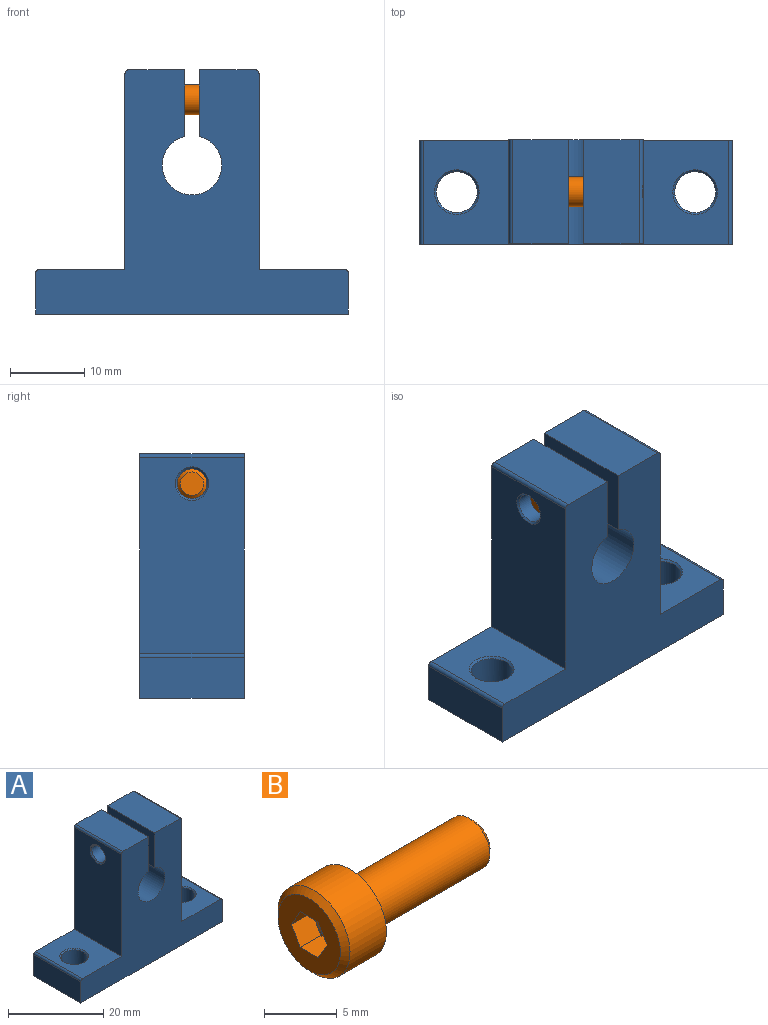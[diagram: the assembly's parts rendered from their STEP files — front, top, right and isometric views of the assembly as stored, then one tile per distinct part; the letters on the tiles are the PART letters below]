
ASSEMBLY  parts=2 mates=1
PART A: 30 faces, bbox 42x14x32.8 mm
  f0: cylinder r=2mm len=4mm, axis (1,0,0), area 50.3mm2, adj f11,f22
  f1: plane 42x14mm, normal (0,0,-1), area 531.5mm2, adj f6,f7,f13,f14,f27,f28
  f2: plane 14x8.93mm, normal (1,0,0), area 112.4mm2, adj f3,f12,f13,f14,f17
  f3: plane 14x7.5mm, normal (0,0,1), area 105mm2, adj f2,f13,f14,f18
  f4: plane 26.3x14mm, normal (-1,0,0), area 352.3mm2, adj f5,f13,f14,f18,f26
  f5: plane 14x11.5mm, normal (0,0,1), area 132.7mm2, adj f4,f13,f14,f19,f25
  f6: plane 14x5.5mm, normal (-1,0,0), area 77mm2, adj f1,f13,f14,f19
  f7: plane 14x5.5mm, normal (1,0,0), area 77mm2, adj f1,f13,f14,f20
  f8: plane 14x11.5mm, normal (0,0,1), area 132.7mm2, adj f9,f13,f14,f20,f24
  f9: plane 26.3x14mm, normal (1,0,0), area 324.5mm2, adj f8,f13,f14,f21,f29
  f10: plane 14x7.5mm, normal (0,0,1), area 105mm2, adj f11,f13,f14,f21
  f11: plane 14x8.93mm, normal (-1,0,0), area 112.4mm2, adj f0,f10,f12,f13,f14
  f12: cylinder r=4mm len=14mm, axis (0,1,0), area 323.6mm2, adj f2,f11,f13,f14
  f13: plane 42x32.8mm, normal (0,-1,0), area 666.2mm2, adj f1,f2,f3,f4,f5,f6,f7,f8
  f14: plane 42x32.8mm, normal (0,1,0), area 666.2mm2, adj f1,f2,f3,f4,f5,f6,f7,f8
  f15: cylinder r=2.75mm len=5.5mm, axis (0,0,-1), area 95mm2, adj f24,f28
  f16: cylinder r=2.75mm len=5.5mm, axis (0,0,-1), area 95mm2, adj f25,f27
  f17: cylinder r=2mm len=7.75mm, axis (1,0,0), area 97.4mm2, adj f2,f26
  f18: cylinder r=0.5mm len=14mm, axis (0,1,0), area 11mm2, adj f3,f4,f13,f14
  f19: cylinder r=0.5mm len=14mm, axis (0,1,0), area 11mm2, adj f5,f6,f13,f14
  f20: cylinder r=0.5mm len=14mm, axis (0,1,0), area 11mm2, adj f7,f8,f13,f14
  f21: cylinder r=0.5mm len=14mm, axis (0,1,0), area 10.6mm2, adj f9,f10,f13,f14,f29
  f22: plane 7x7mm, normal (1,0,0), area 25.9mm2, adj f0,f23
  f23: cylinder r=3.5mm len=7mm, axis (1,0,0), area 82.5mm2, adj f22,f29
  f24: cone r=3mm half-angle=45deg, axis (0,0,1), area 6.4mm2, adj f8,f15
  f25: cone r=3mm half-angle=45deg, axis (0,0,1), area 6.4mm2, adj f5,f16
  f26: cone r=2.25mm half-angle=45deg, axis (-1,0,0), area 4.7mm2, adj f4,f17
  f27: cone r=2.75mm half-angle=45deg, axis (0,0,-1), area 6.4mm2, adj f1,f16
  f28: cone r=3mm half-angle=45deg, axis (0,0,-1), area 6.4mm2, adj f1,f15
  f29: cone r=3.5mm half-angle=45deg, axis (1,0,0), area 8mm2, adj f9,f21,f23
PART B: 21 faces, bbox 16x7x7 mm
  f0: plane 6.07x6.07mm, normal (-1,0,0), area 21.1mm2, adj f1,f13,f14,f15,f16,f17,f18
  f1: cone r=3.03mm half-angle=45deg, axis (1,0,0), area 13.5mm2, adj f0,f2
  f2: cylinder r=3.5mm len=7mm, axis (1,0,0), area 77.7mm2, adj f1,f3
  f3: plane 7x7mm, normal (1,0,0), area 25.9mm2, adj f2,f4
  f4: cylinder r=2mm len=11.57mm, axis (1,0,0), area 145.4mm2, adj f3,f5
  f5: cone r=2mm half-angle=45deg, axis (-1,0,0), area 6.8mm2, adj f4,f6
  f6: plane 3.14x3.14mm, normal (1,0,0), area 7.7mm2, adj f5
  f7: plane 1.3x0.75mm, normal (-1,0,0), area 0.1mm2, adj f15,f16,f20
  f8: plane 1.5x0.43mm, normal (-1,0,0), area 0.1mm2, adj f14,f15,f20
  f9: plane 1.3x0.75mm, normal (-1,0,0), area 0.1mm2, adj f13,f14,f20
  f10: plane 1.3x0.75mm, normal (-1,0,0), area 0.1mm2, adj f13,f18,f20
  f11: plane 1.5x0.43mm, normal (-1,0,0), area 0.1mm2, adj f17,f18,f20
  f12: plane 1.3x0.75mm, normal (-1,0,0), area 0.1mm2, adj f16,f17,f20
  f13: plane 2x1.73mm, normal (0,0,-1), area 3.5mm2, adj f0,f9,f10,f14,f18
  f14: plane 2x1.5mm, normal (0,0.87,-0.5), area 3.5mm2, adj f0,f8,f9,f13,f15
  f15: plane 2x1.5mm, normal (0,0.87,0.5), area 3.5mm2, adj f0,f7,f8,f14,f16
  f16: plane 2x1.73mm, normal (0,0,1), area 3.5mm2, adj f0,f7,f12,f15,f17
  f17: plane 2x1.5mm, normal (0,-0.87,0.5), area 3.5mm2, adj f0,f11,f12,f16,f18
  f18: plane 2x1.5mm, normal (0,-0.87,-0.5), area 3.5mm2, adj f0,f10,f11,f13,f17
  f19: cone r=0mm half-angle=75deg, axis (-1,0,0), area 7.3mm2, adj f20
  f20: cylinder r=1.5mm len=3mm, axis (1,0,0), area 0mm2, adj f7,f8,f9,f10,f11,f12,f19
PLACE A rot(axis=(0,-1,0),0deg) t=(17.44,-3.31,3.97)mm
PLACE B rot(axis=(0,1,0),180deg) t=(22.44,-3.31,12.77)mm
MATE fastened B.f1 <-> A.f0  axis (-1,0,0) through (22.44,-3.31,12.77)mm
